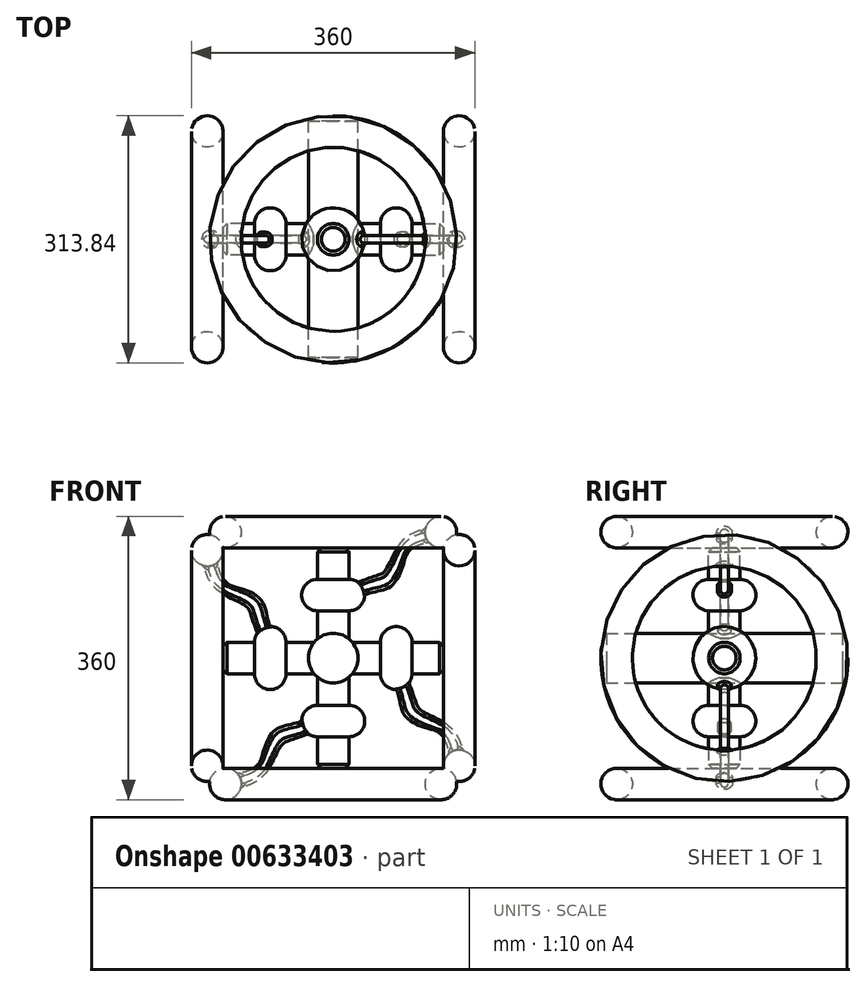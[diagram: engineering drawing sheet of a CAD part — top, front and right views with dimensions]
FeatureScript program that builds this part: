
annotation { "Feature Type Name" : "Feature", "Feature Type Description" : "" }
export const myFeature = defineFeature(function(context is Context, id is Id, definition is map)
    precondition{}
    {
        {
            var Q0;
            Q0=qCreatedBy(makeId("Front.planeOp"),FACE);
            var sketch = newSketch(context, id + "F0", { "sketchPlane" : qUnion([Q0])});
            skLineSegment(sketch, "E0", {"start": v(0, 60) * mm, "end": v(0, -60) * mm});
            skLineSegment(sketch, "E1", {"start": v(0, -60) * mm, "end": v(20, -60) * mm});
            skLineSegment(sketch, "E2", {"start": v(20, -60) * mm, "end": v(20, -20) * mm});
            skLineSegment(sketch, "E3", {"start": v(0, 60) * mm, "end": v(20, 60) * mm});
            skLineSegment(sketch, "E4", {"start": v(20, 60) * mm, "end": v(20, 20) * mm});
            skArc(sketch, "E5", {"start": v(20, -20) * mm, "mid": v(40, 0) * mm, "end": v(20, 20) * mm});
            skSolve(sketch);
        }
        {
            var Q0;
            Q0=makeQuery(id+"F0.imprint","IMPRINT",FACE,{"disambiguationData":[TD([[makeQuery(id+"F0.imprint","IMPRINT",EDGE,{"derivedFrom":sQuery(id+"F0.wireOp",EDGE,"E0")}),1.0]])]});
            var Q1;
            Q1=sQuery(id+"F0.wireOp",EDGE,"E0");
            revolve(context, id + "F1", {"entities" : qUnion([Q0]), "axis" : qUnion([Q1]), "revolveType" : RevolveType.FULL});
        }
        {
            var Q0;
            Q0=makeQuery(id+"F1.opRevolve","SWEPT_EDGE",EDGE,{"disambiguationData":[OSD([sQuery(id+"F0.wireOp",EDGE,"E3"),sQuery(id+"F0.wireOp",EDGE,"E4")])]});
            var Q1;
            Q1=makeQuery(id+"F1.opRevolve","SWEPT_EDGE",EDGE,{"disambiguationData":[OSD([sQuery(id+"F0.wireOp",EDGE,"E1"),sQuery(id+"F0.wireOp",EDGE,"E2")])]});
            chamfer(context, id + "F2", {"entities" : qUnion([Q0, Q1]), "width" : 5 * mm, "tangentPropagation" : true});
        }
        {
            var Q0;
            Q0=qCreatedBy(makeId("Right.planeOp"),FACE);
            cPlane(context, id + "F3", {"entities" : qUnion([Q0]), "cplaneType" : CPlaneType.OFFSET, "offset" : 20 * mm, "width" : 150 * mm, "height" : 150 * mm});
        }
        {
            var Q0;
            Q0=qCreatedBy(id+"F3.planeOp",FACE);
            var sketch = newSketch(context, id + "F4", { "sketchPlane" : qUnion([Q0])});
            skLineSegment(sketch, "E6.bottom", {"start": v(0, 10) * mm, "end": v(0, 10) * mm});
            skLineSegment(sketch, "E6.top", {"start": v(0, -10) * mm, "end": v(0, -10) * mm});
            skLineSegment(sketch, "E6.left", {"start": v(5, 5) * mm, "end": v(5, -5) * mm});
            skLineSegment(sketch, "E6.right", {"start": v(-5, 5) * mm, "end": v(-5, -5) * mm});
            skPoint(sketch, "E6.middle", {"position": v(0, 0) * mm});
            skPoint(sketch, "E7.visualSharp", {"position": v(-5, 10) * mm});
            skArc(sketch, "E7.filletArc", {"start": v(0, 10) * mm, "mid": v(-3.54, 8.54) * mm, "end": v(-5, 5) * mm});
            skPoint(sketch, "E8.visualSharp", {"position": v(5, -10) * mm});
            skArc(sketch, "E8.filletArc", {"start": v(0, -10) * mm, "mid": v(3.54, -8.54) * mm, "end": v(5, -5) * mm});
            skPoint(sketch, "E9.visualSharp", {"position": v(5, 10) * mm});
            skArc(sketch, "E9.filletArc", {"start": v(5, 5) * mm, "mid": v(4.22, 7.68) * mm, "end": v(2.14, 9.52) * mm});
            skArc(sketch, "E10.filletArc", {"start": v(2.14, 9.52) * mm, "mid": v(-2.68, 9.22) * mm, "end": v(-5, 5) * mm});
            skPoint(sketch, "E11.visualSharp", {"position": v(-5, -10) * mm});
            skArc(sketch, "E11.filletArc", {"start": v(-5, -5) * mm, "mid": v(-3.54, -8.54) * mm, "end": v(0, -10) * mm});
            skSolve(sketch);
        }
        {
            var Q0;
            Q0=qCreatedBy(makeId("Front.planeOp"),FACE);
            var sketch = newSketch(context, id + "F5", { "sketchPlane" : qUnion([Q0])});
            skFitSpline(sketch, "E12", {"points": [v(32.74, 0) * mm, v(76.28, 21.38) * mm, v(100.66, 60.08) * mm, v(150, 79.95) * mm], "startDerivative": vector(154.14, 80.47) * mm, "endDerivative": vector(168.8, 75.3) * mm});
            skSolve(sketch);
        }
        {
            var Q0;
            Q0 = qSketchRegion(id + "F4", true);
            var Q1;
            Q1 = qConstructionFilter(qBodyType(qCreatedBy(id + "F5" ,EDGE), BodyType.WIRE), ConstructionObject.NO);
            sweep(context, id + "F6", {"operationType" : NewBodyOperationType.ADD, "profiles" : qUnion([Q0]), "path" : qUnion([Q1])});
        }
        {
            var Q0;
            Q0=qCreatedBy(makeId("Front.planeOp"),FACE);
            var sketch = newSketch(context, id + "F7", { "sketchPlane" : qUnion([Q0])});
            skCircle(sketch, "E13", {"center": v(136.92, 80) * mm, "radius": 20 * mm});
            skSolve(sketch);
        }
        {
            var Q0;
            Q0=makeQuery(id+"F7.imprint","IMPRINT",FACE,{"disambiguationData":[TD([[makeQuery(id+"F7.imprint","IMPRINT",EDGE,{"derivedFrom":sQuery(id+"F7.wireOp",EDGE,"E13")}),1.0]])]});
            var Q1;
            Q1=makeQuery(id+"F1.opRevolve","SWEPT_FACE",FACE,{"disambiguationData":[OSD([sQuery(id+"F0.wireOp",EDGE,"E4")])]});
            revolve(context, id + "F8", {"operationType" : NewBodyOperationType.ADD, "entities" : qUnion([Q0]), "axis" : qUnion([Q1]), "revolveType" : RevolveType.FULL});
        }
        {
            var Q0;
            Q0=makeQuery(id+"F8.boolean.opBoolean","INTERSECT",EDGE,{"derivedFrom":[makeQuery(id+"FWwjdPsJzfJvs70_1.4.F6.opSweep","SWEPT_FACE",FACE,{"disambiguationData":[OSD([sQuery(id+"F4.wireOp",EDGE,"E9.filletArc"),sQuery(id+"F4.wireOp",EDGE,"E10.filletArc"),sQuery(id+"F5.wireOp",EDGE,"E12")])]}),makeQuery(id+"F8.opRevolve","SWEPT_FACE",FACE,{"disambiguationData":[OSD([sQuery(id+"F7.wireOp",EDGE,"E13")])]})]});
            var Q1;
            Q1=makeQuery(id+"F8.boolean.opBoolean","INTERSECT",EDGE,{"derivedFrom":[makeQuery(id+"F6.opSweep","SWEPT_FACE",FACE,{"disambiguationData":[OSD([sQuery(id+"F4.wireOp",EDGE,"E9.filletArc"),sQuery(id+"F4.wireOp",EDGE,"E10.filletArc"),sQuery(id+"F5.wireOp",EDGE,"E12")])]}),makeQuery(id+"F8.opRevolve","SWEPT_FACE",FACE,{"disambiguationData":[OSD([sQuery(id+"F7.wireOp",EDGE,"E13")])]})]});
            var Q2;
            Q2=makeQuery(id+"F8.boolean.opBoolean","INTERSECT",EDGE,{"derivedFrom":[makeQuery(id+"FWwjdPsJzfJvs70_1.3.F6.opSweep","SWEPT_FACE",FACE,{"disambiguationData":[OSD([sQuery(id+"F4.wireOp",EDGE,"E9.filletArc"),sQuery(id+"F4.wireOp",EDGE,"E10.filletArc"),sQuery(id+"F5.wireOp",EDGE,"E12")])]}),makeQuery(id+"F8.opRevolve","SWEPT_FACE",FACE,{"disambiguationData":[OSD([sQuery(id+"F7.wireOp",EDGE,"E13")])]})]});
            var Q3;
            Q3=makeQuery(id+"F8.boolean.opBoolean","INTERSECT",EDGE,{"derivedFrom":[makeQuery(id+"FWwjdPsJzfJvs70_1.2.F6.opSweep","SWEPT_FACE",FACE,{"disambiguationData":[OSD([sQuery(id+"F4.wireOp",EDGE,"E9.filletArc"),sQuery(id+"F4.wireOp",EDGE,"E10.filletArc"),sQuery(id+"F5.wireOp",EDGE,"E12")])]}),makeQuery(id+"F8.opRevolve","SWEPT_FACE",FACE,{"disambiguationData":[OSD([sQuery(id+"F7.wireOp",EDGE,"E13")])]})]});
            var Q4;
            Q4=makeQuery(id+"F8.boolean.opBoolean","INTERSECT",EDGE,{"derivedFrom":[makeQuery(id+"FWwjdPsJzfJvs70_1.1.F6.opSweep","SWEPT_FACE",FACE,{"disambiguationData":[OSD([sQuery(id+"F4.wireOp",EDGE,"E9.filletArc"),sQuery(id+"F4.wireOp",EDGE,"E10.filletArc"),sQuery(id+"F5.wireOp",EDGE,"E12")])]}),makeQuery(id+"F8.opRevolve","SWEPT_FACE",FACE,{"disambiguationData":[OSD([sQuery(id+"F7.wireOp",EDGE,"E13")])]})]});
            fillet(context, id + "F9", {"entities" : qUnion([Q0, Q1, Q2, Q3, Q4]), "radius" : 5 * mm, "tangentPropagation" : true, "allowEdgeOverflow" : false});
        }
        {
            var Q0;
            Q0=makeQuery(id+"FWwjdPsJzfJvs70_1.4.F6.boolean.opBoolean","INTERSECT",EDGE,{"derivedFrom":[makeQuery(id+"F1.opRevolve","SWEPT_FACE",FACE,{"disambiguationData":[OSD([sQuery(id+"F0.wireOp",EDGE,"E5")])]}),makeQuery(id+"FWwjdPsJzfJvs70_1.4.F6.opSweep","SWEPT_FACE",FACE,{"disambiguationData":[OSD([sQuery(id+"F4.wireOp",EDGE,"E9.filletArc"),sQuery(id+"F4.wireOp",EDGE,"E10.filletArc"),sQuery(id+"F5.wireOp",EDGE,"E12")])]})]});
            var Q1;
            Q1=makeQuery(id+"FWwjdPsJzfJvs70_1.3.F6.boolean.opBoolean","INTERSECT",EDGE,{"derivedFrom":[makeQuery(id+"F1.opRevolve","SWEPT_FACE",FACE,{"disambiguationData":[OSD([sQuery(id+"F0.wireOp",EDGE,"E5")])]}),makeQuery(id+"FWwjdPsJzfJvs70_1.3.F6.opSweep","SWEPT_FACE",FACE,{"disambiguationData":[OSD([sQuery(id+"F4.wireOp",EDGE,"E9.filletArc"),sQuery(id+"F4.wireOp",EDGE,"E10.filletArc"),sQuery(id+"F5.wireOp",EDGE,"E12")])]})]});
            var Q2;
            Q2=makeQuery(id+"FWwjdPsJzfJvs70_1.2.F6.boolean.opBoolean","INTERSECT",EDGE,{"derivedFrom":[makeQuery(id+"F1.opRevolve","SWEPT_FACE",FACE,{"disambiguationData":[OSD([sQuery(id+"F0.wireOp",EDGE,"E5")])]}),makeQuery(id+"FWwjdPsJzfJvs70_1.2.F6.opSweep","SWEPT_FACE",FACE,{"disambiguationData":[OSD([sQuery(id+"F4.wireOp",EDGE,"E9.filletArc"),sQuery(id+"F4.wireOp",EDGE,"E10.filletArc"),sQuery(id+"F5.wireOp",EDGE,"E12")])]})]});
            var Q3;
            Q3=makeQuery(id+"FWwjdPsJzfJvs70_1.1.F6.boolean.opBoolean","INTERSECT",EDGE,{"derivedFrom":[makeQuery(id+"F1.opRevolve","SWEPT_FACE",FACE,{"disambiguationData":[OSD([sQuery(id+"F0.wireOp",EDGE,"E5")])]}),makeQuery(id+"FWwjdPsJzfJvs70_1.1.F6.opSweep","SWEPT_FACE",FACE,{"disambiguationData":[OSD([sQuery(id+"F4.wireOp",EDGE,"E9.filletArc"),sQuery(id+"F4.wireOp",EDGE,"E10.filletArc"),sQuery(id+"F5.wireOp",EDGE,"E12")])]})]});
            var Q4;
            Q4=makeQuery(id+"F6.boolean.opBoolean","INTERSECT",EDGE,{"derivedFrom":[makeQuery(id+"F1.opRevolve","SWEPT_FACE",FACE,{"disambiguationData":[OSD([sQuery(id+"F0.wireOp",EDGE,"E5")])]}),makeQuery(id+"F6.opSweep","SWEPT_FACE",FACE,{"disambiguationData":[OSD([sQuery(id+"F4.wireOp",EDGE,"E9.filletArc"),sQuery(id+"F4.wireOp",EDGE,"E10.filletArc"),sQuery(id+"F5.wireOp",EDGE,"E12")])]})]});
            fillet(context, id + "F10", {"entities" : qUnion([Q0, Q1, Q2, Q3, Q4]), "radius" : 5 * mm, "tangentPropagation" : true, "allowEdgeOverflow" : false});
        }
        {
            var Q0;
            Q0=qCreatedBy(makeId("Front.planeOp"),FACE);
            var sketch = newSketch(context, id + "F11", { "sketchPlane" : qUnion([Q0])});
            skCircle(sketch, "E14", {"center": v(0, -80) * mm, "radius": 31.5 * mm});
            skSolve(sketch);
        }
        {
            var Q0;
            Q0=makeQuery(id+"F11.imprint","IMPRINT",FACE,{"disambiguationData":[TD([[makeQuery(id+"F11.imprint","IMPRINT",EDGE,{"derivedFrom":sQuery(id+"F11.wireOp",EDGE,"E14")}),1.0]])]});
            extrude(context, id + "F12", {"entities" : qUnion([Q0]), "operationType" : NewBodyOperationType.ADD, "endBound" : BoundingType.SYMMETRIC, "depth" : 300 * mm, "offsetDistance" : 25 * mm});
        }
        {
            var Q0;
            Q0=makeQuery(id+"F1.opRevolve","SWEPT_BODY",BODY,{"disambiguationData":[OSD([sQuery(id+"F0.wireOp",EDGE,"E0"),sQuery(id+"F0.wireOp",EDGE,"E1"),sQuery(id+"F0.wireOp",EDGE,"E2"),sQuery(id+"F0.wireOp",EDGE,"E3"),sQuery(id+"F0.wireOp",EDGE,"E4"),sQuery(id+"F0.wireOp",EDGE,"E5")])]});
            var Q1;
            Q1=makeQuery(id+"F12.opExtrude","SWEPT_FACE",FACE,{"disambiguationData":[OSD([sQuery(id+"F11.wireOp",EDGE,"E14")])]});
            circularPattern(context, id + "F13", {"entities" : qUnion([Q0]), "axis" : qUnion([Q1]), "angle" : 360 * degree, "instanceCount" : 4, "equalSpace" : true});
        }
    });
